# Revit family: Krome C9071-C9076 Series
name_source: partatom
category: Plumbing Fixtures
revit_build: Autodesk Revit 2018 (Build: 20181015_0930(x64)
units: mm (PartAtom-declared; Revit-internal decimal feet)

## family parameters
Always vertical = Yes
Cut with Voids When Loaded = No
Part Type = Normal
Room Calculation Point = No
Round Connector Dimension = Use Diameter
Shared = No
Work Plane-Based = No

## types (6) — shared parameters
URL = https://kromedispense.co.in

## per-type parameters (varying)
| type | Grab Bar Length | Model | Weight (lbs) |
| C9071-9" Commercial Peened Wall Mount Grab Bars | 0' - 9" | C9071 Series | .84 |
| C9072-12" Commercial Peened Wall Mount Grab Bars | 1' - 0" | C9072 Series | 0.99 |
| C9073-18" Commercial Peened Wall Mount Grab Bars | 1' - 6" | C9073 Series | 1.30 |
| C9074-24" Commercial Peened Wall Mount Grab Bars | 2' - 0" | C9074 Series | 1.61 |
| C9075-36" Commercial Peened Wall Mount Grab Bars | 3' - 0" | C9075 Series | 2.23 |
| C9076-48" Commercial Peened Wall Mount Grab Bars | 4' - 0" | C9076 Series | 2.85 |

## geometry (parser evidence)
native form markers: Sweep x3
no freeform markers — native parametric forms only
